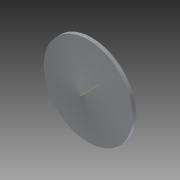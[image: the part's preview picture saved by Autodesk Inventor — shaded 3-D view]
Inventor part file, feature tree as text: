
AUTODESK INVENTOR PART (.ipt)
format: ipt  version: 2014 (Build 180170000, 170)  size: 84,480 bytes
history: native  units: mm
features: revolve x1, sketch x1
ambient origin geometry x8: Origin, YZ Plane, XZ Plane, XY Plane, X Axis, Y Axis, Z Axis, Center Point
bodies: Solid1 (feature_tree)
feature tree (2):
  revolve  "Revolution1"  [1 undecoded]
  sketch  "Sketch1"  dims[d0=50.0mm d1=9.0mm d2=2.0mm d3=90.0deg]
note: 1 required parameter value undecoded (feature->parameter linkage not recoverable at this tier; creation-order binding heuristic only, values carry confidence <= 0.55)
